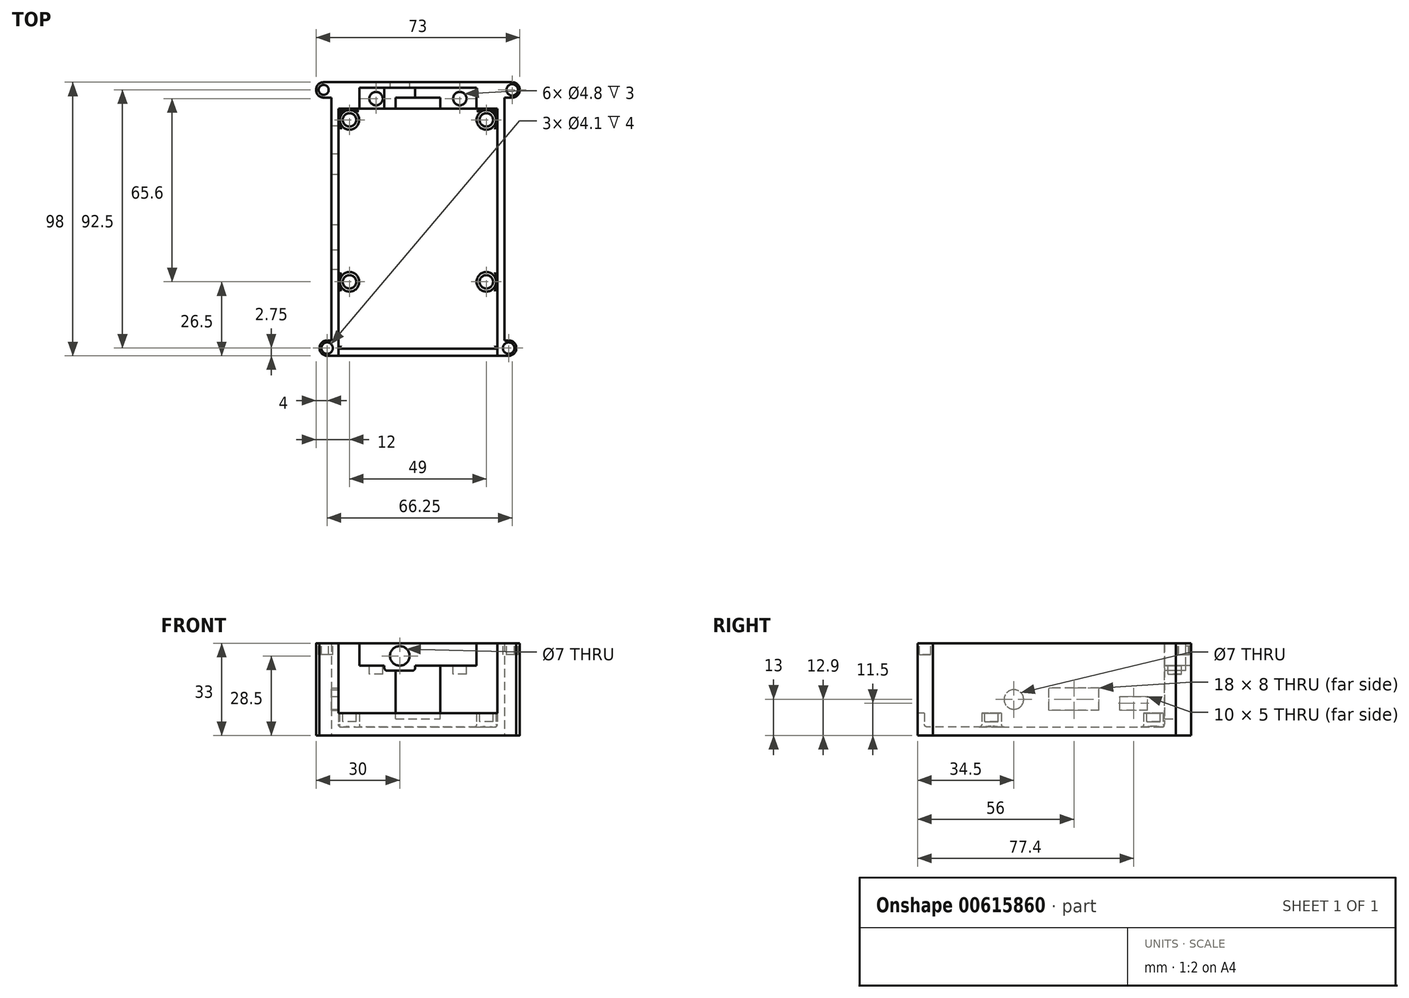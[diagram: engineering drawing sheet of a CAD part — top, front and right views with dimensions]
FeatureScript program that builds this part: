
annotation { "Feature Type Name" : "Feature", "Feature Type Description" : "" }
export const myFeature = defineFeature(function(context is Context, id is Id, definition is map)
    precondition{}
    {
        {
            var Q0;
            Q0=qCreatedBy(makeId("Top.planeOp"),FACE);
            var sketch = newSketch(context, id + "F0", { "sketchPlane" : qUnion([Q0])});
            skLineSegment(sketch, "E0.bottom", {"start": v(25, -42.5) * mm, "end": v(-28, -42.5) * mm, "construction": true});
            skLineSegment(sketch, "E0.top", {"start": v(25, 42.5) * mm, "end": v(-25, 42.5) * mm, "construction": true});
            skLineSegment(sketch, "E0.left", {"start": v(28, -39.5) * mm, "end": v(28, 39.5) * mm, "construction": true});
            skLineSegment(sketch, "E0.right", {"start": v(-28, -42.5) * mm, "end": v(-28, 39.5) * mm, "construction": true});
            skPoint(sketch, "E0.middle", {"position": v(0, 0) * mm});
            skLineSegment(sketch, "E1.0", {"start": v(31, -45.5) * mm, "end": v(-31, -45.5) * mm});
            skLineSegment(sketch, "E1.1", {"start": v(31, -45.5) * mm, "end": v(31, 45.5) * mm});
            skLineSegment(sketch, "E1.2", {"start": v(31, 45.5) * mm, "end": v(-31, 45.5) * mm});
            skLineSegment(sketch, "E1.3", {"start": v(-31, -45.5) * mm, "end": v(-31, 45.5) * mm});
            skPoint(sketch, "E2.visualSharp", {"position": v(28, -42.5) * mm});
            skArc(sketch, "E2.filletArc", {"start": v(25, -42.5) * mm, "mid": v(27.12, -41.62) * mm, "end": v(28, -39.5) * mm, "construction": true});
            skPoint(sketch, "E3.visualSharp", {"position": v(-28, -42.5) * mm});
            skPoint(sketch, "E4.visualSharp", {"position": v(-28, 42.5) * mm});
            skArc(sketch, "E4.filletArc", {"start": v(-25, 42.5) * mm, "mid": v(-27.12, 41.62) * mm, "end": v(-28, 39.5) * mm, "construction": true});
            skPoint(sketch, "E5.visualSharp", {"position": v(28, 42.5) * mm});
            skArc(sketch, "E5.filletArc", {"start": v(28, 39.5) * mm, "mid": v(27.12, 41.62) * mm, "end": v(25, 42.5) * mm, "construction": true});
            skSolve(sketch);
        }
        {
            var Q0;
            Q0 = qSketchRegion(id + "F0", true);
            extrude(context, id + "F1", {"entities" : qUnion([Q0]), "depth" : 3 * mm, "offsetDistance" : 25 * mm});
        }
        {
            var Q0;
            Q0=makeQuery(id+"F1.opExtrude","CAP_FACE",FACE,{"disambiguationData":[OSD([sQuery(id+"F0.wireOp",EDGE,"E1.0"),sQuery(id+"F0.wireOp",EDGE,"E1.1"),sQuery(id+"F0.wireOp",EDGE,"E1.2"),sQuery(id+"F0.wireOp",EDGE,"E1.3")])],"isStart":false});
            var sketch = newSketch(context, id + "F2", { "sketchPlane" : qUnion([Q0])});
            skLineSegment(sketch, "E6.0", {"start": v(-28.5, 43) * mm, "end": v(-28.5, -43) * mm});
            skLineSegment(sketch, "E6.1", {"start": v(28.5, 43) * mm, "end": v(-28.5, 43) * mm});
            skLineSegment(sketch, "E6.2", {"start": v(28.5, -43) * mm, "end": v(28.5, 43) * mm});
            skLineSegment(sketch, "E6.3", {"start": v(-28.5, -43) * mm, "end": v(28.5, -43) * mm});
            skLineSegment(sketch, "E7.bottom", {"start": v(-31, 45.5) * mm, "end": v(31, 45.5) * mm});
            skLineSegment(sketch, "E7.top", {"start": v(-31, -45.5) * mm, "end": v(31, -45.5) * mm});
            skLineSegment(sketch, "E7.left", {"start": v(-31, 45.5) * mm, "end": v(-31, -45.5) * mm});
            skLineSegment(sketch, "E7.right", {"start": v(31, 45.5) * mm, "end": v(31, -45.5) * mm});
            skSolve(sketch);
        }
        {
            var Q0;
            Q0 = qSketchRegion(id + "F2", true);
            extrude(context, id + "F3", {"entities" : qUnion([Q0]), "operationType" : NewBodyOperationType.ADD, "depth" : 30 * mm, "offsetDistance" : 25 * mm});
        }
        {
            var Q0;
            Q0=makeQuery(id+"F1.opExtrude","CAP_FACE",FACE,{"disambiguationData":[OSD([sQuery(id+"F0.wireOp",EDGE,"E1.0"),sQuery(id+"F0.wireOp",EDGE,"E1.1"),sQuery(id+"F0.wireOp",EDGE,"E1.2"),sQuery(id+"F0.wireOp",EDGE,"E1.3")])],"isStart":false});
            var sketch = newSketch(context, id + "F4", { "sketchPlane" : qUnion([Q0])});
            skCircle(sketch, "E8", {"center": v(-24.5, 39) * mm, "radius": 3.5 * mm});
            skCircle(sketch, "E9", {"center": v(24.5, 39) * mm, "radius": 3.5 * mm});
            skCircle(sketch, "E10", {"center": v(-24.5, -19) * mm, "radius": 3.5 * mm});
            skCircle(sketch, "E11", {"center": v(24.5, -19) * mm, "radius": 3.5 * mm});
            skSolve(sketch);
        }
        {
            var Q0;
            Q0 = qSketchRegion(id + "F4", true);
            extrude(context, id + "F5", {"entities" : qUnion([Q0]), "operationType" : NewBodyOperationType.ADD, "depth" : 5 * mm, "offsetDistance" : 25 * mm});
        }
        {
            var Q0;
            Q0=makeQuery(id+"F5.opExtrude","CAP_FACE",FACE,{"disambiguationData":[OSD([sQuery(id+"F4.wireOp",EDGE,"E9")])],"isStart":false});
            var sketch = newSketch(context, id + "F6", { "sketchPlane" : qUnion([Q0])});
            skCircle(sketch, "E12", {"center": v(-24.5, 39) * mm, "radius": 2.4 * mm});
            skCircle(sketch, "E13", {"center": v(24.5, 39) * mm, "radius": 2.4 * mm});
            skCircle(sketch, "E14", {"center": v(-24.5, -19) * mm, "radius": 2.4 * mm});
            skCircle(sketch, "E15", {"center": v(24.5, -19) * mm, "radius": 2.4 * mm});
            skSolve(sketch);
        }
        {
            var Q0;
            Q0 = qSketchRegion(id + "F6", true);
            extrude(context, id + "F7", {"entities" : qUnion([Q0]), "operationType" : NewBodyOperationType.REMOVE, "oppositeDirection" : true, "depth" : 3 * mm, "offsetDistance" : 25 * mm});
        }
        {
            var Q0;
            Q0=makeQuery(id+"F3.boolean.opBoolean","MERGE",FACE,{"derivedFrom":[makeQuery(id+"F1.opExtrude","SWEPT_FACE",FACE,{"disambiguationData":[OSD([sQuery(id+"F0.wireOp",EDGE,"E1.0")])]}),makeQuery(id+"F3.opExtrude","SWEPT_FACE",FACE,{"disambiguationData":[OSD([sQuery(id+"F2.wireOp",EDGE,"E7.top")])]})]});
            var sketch = newSketch(context, id + "F8", { "sketchPlane" : qUnion([Q0])});
            skLineSegment(sketch, "E16", {"start": v(-28.5, 8) * mm, "end": v(28.5, 8) * mm});
            skLineSegment(sketch, "E17", {"start": v(28.5, 8) * mm, "end": v(28.5, 33) * mm});
            skLineSegment(sketch, "E18", {"start": v(-28.5, 8) * mm, "end": v(-28.5, 33) * mm});
            skLineSegment(sketch, "E19", {"start": v(28.5, 33) * mm, "end": v(-28.5, 33) * mm});
            skSolve(sketch);
        }
        {
            var Q0;
            Q0 = qSketchRegion(id + "F8", true);
            var Q1;
            Q1=makeQuery(id+"F3.opExtrude","SWEPT_FACE",FACE,{"disambiguationData":[OSD([sQuery(id+"F2.wireOp",EDGE,"E6.3")])]});
            extrude(context, id + "F9", {"entities" : qUnion([Q0]), "operationType" : NewBodyOperationType.REMOVE, "endBound" : BoundingType.UP_TO_SURFACE, "oppositeDirection" : true, "depth" : 25 * mm, "endBoundEntityFace" : qUnion([Q1]), "offsetDistance" : 25 * mm});
        }
        {
            var Q0;
            Q0=makeQuery(id+"F3.opExtrude","SWEPT_FACE",FACE,{"disambiguationData":[OSD([sQuery(id+"F2.wireOp",EDGE,"E6.0")])]});
            var sketch = newSketch(context, id + "F10", { "sketchPlane" : qUnion([Q0])});
            skLineSegment(sketch, "E20.bottom", {"start": v(36.9, 9) * mm, "end": v(26.9, 9) * mm});
            skLineSegment(sketch, "E20.left", {"start": v(36.9, 9) * mm, "end": v(36.9, 14) * mm});
            skLineSegment(sketch, "E20.right", {"start": v(26.9, 9) * mm, "end": v(26.9, 14) * mm});
            skLineSegment(sketch, "E21", {"start": v(42.5, 25.13) * mm, "end": v(42.5, 0) * mm, "construction": true});
            skLineSegment(sketch, "E22.bottom", {"start": v(19.5, 9) * mm, "end": v(1.5, 9) * mm});
            skLineSegment(sketch, "E22.top", {"start": v(19.5, 17) * mm, "end": v(1.5, 17) * mm});
            skLineSegment(sketch, "E22.left", {"start": v(19.5, 9) * mm, "end": v(19.5, 17) * mm});
            skLineSegment(sketch, "E22.right", {"start": v(1.5, 9) * mm, "end": v(1.5, 17) * mm});
            skLineSegment(sketch, "E23", {"start": v(26.9, 14) * mm, "end": v(31.9, 14) * mm});
            skLineSegment(sketch, "E24", {"start": v(31.9, 14) * mm, "end": v(36.9, 14) * mm});
            skLineSegment(sketch, "E25", {"start": v(10.5, 17) * mm, "end": v(10.5, 23.95) * mm, "construction": true});
            skPoint(sketch, "E25.endSnap0", {"position": v(10.5, 17) * mm});
            skLineSegment(sketch, "E26", {"start": v(26.9, 9) * mm, "end": v(19.5, 9) * mm, "construction": true});
            skCircle(sketch, "E27", {"center": v(-11, 12.9) * mm, "radius": 3.5 * mm});
            skSolve(sketch);
        }
        {
            var Q0;
            Q0 = qSketchRegion(id + "F10", true);
            var Q1;
            Q1=makeQuery(id+"F3.boolean.opBoolean","MERGE",FACE,{"derivedFrom":[makeQuery(id+"F1.opExtrude","SWEPT_FACE",FACE,{"disambiguationData":[OSD([sQuery(id+"F0.wireOp",EDGE,"E1.3")])]}),makeQuery(id+"F3.opExtrude","SWEPT_FACE",FACE,{"disambiguationData":[OSD([sQuery(id+"F2.wireOp",EDGE,"E7.left")])]})]});
            extrude(context, id + "F11", {"entities" : qUnion([Q0]), "operationType" : NewBodyOperationType.REMOVE, "endBound" : BoundingType.UP_TO_SURFACE, "oppositeDirection" : true, "depth" : 25 * mm, "endBoundEntityFace" : qUnion([Q1]), "offsetDistance" : 25 * mm});
        }
        {
            var Q0;
            Q0=makeQuery(id+"F3.boolean.opBoolean","MERGE",FACE,{"derivedFrom":[makeQuery(id+"F1.opExtrude","SWEPT_FACE",FACE,{"disambiguationData":[OSD([sQuery(id+"F0.wireOp",EDGE,"E1.2")])]}),makeQuery(id+"F3.opExtrude","SWEPT_FACE",FACE,{"disambiguationData":[OSD([sQuery(id+"F2.wireOp",EDGE,"E7.bottom")])]})]});
            extrude(context, id + "F12", {"entities" : qUnion([Q0]), "operationType" : NewBodyOperationType.ADD, "depth" : 7 * mm, "offsetDistance" : 25 * mm});
        }
        {
            var Q0;
            {var subQ0=sQuery(id+"F2.wireOp",EDGE,"E7.bottom");Q0=makeQuery(id+"F12.boolean.opBoolean","MERGE",FACE,{"derivedFrom":[makeQuery(id+"F3.opExtrude","CAP_FACE",FACE,{"disambiguationData":[OSD([sQuery(id+"F2.wireOp",EDGE,"E6.0"),sQuery(id+"F2.wireOp",EDGE,"E6.1"),sQuery(id+"F2.wireOp",EDGE,"E6.2"),sQuery(id+"F2.wireOp",EDGE,"E6.3"),subQ0,sQuery(id+"F2.wireOp",EDGE,"E7.top"),sQuery(id+"F2.wireOp",EDGE,"E7.left"),sQuery(id+"F2.wireOp",EDGE,"E7.right")])],"isStart":false}),makeQuery(id+"F12.opExtrude","SWEPT_FACE",FACE,{"disambiguationData":[OSD([subQ0])]})]});}
            var sketch = newSketch(context, id + "F13", { "sketchPlane" : qUnion([Q0])});
            skLineSegment(sketch, "E28", {"start": v(-21, 43) * mm, "end": v(-21, 50.5) * mm});
            skLineSegment(sketch, "E29", {"start": v(-21, 50.5) * mm, "end": v(21, 50.5) * mm});
            skLineSegment(sketch, "E30", {"start": v(21, 50.5) * mm, "end": v(21, 43) * mm});
            skLineSegment(sketch, "E31", {"start": v(-21, 43) * mm, "end": v(21, 43) * mm});
            skSolve(sketch);
        }
        {
            var Q0;
            Q0 = qSketchRegion(id + "F13", true);
            extrude(context, id + "F14", {"entities" : qUnion([Q0]), "operationType" : NewBodyOperationType.REMOVE, "oppositeDirection" : true, "depth" : 8 * mm, "offsetDistance" : 25 * mm});
        }
        {
            var Q0;
            Q0=makeQuery(id+"F14.boolean.opBoolean","COPY",FACE,{"derivedFrom":makeQuery(id+"F14.opExtrude","CAP_FACE",FACE,{"disambiguationData":[OSD([sQuery(id+"F13.wireOp",EDGE,"E28"),sQuery(id+"F13.wireOp",EDGE,"E29"),sQuery(id+"F13.wireOp",EDGE,"E30"),sQuery(id+"F13.wireOp",EDGE,"Brvc21Z0-0QBP-XG2K-26vJ-c9HecIgVGcnL")])],"isStart":false})});
            var sketch = newSketch(context, id + "F15", { "sketchPlane" : qUnion([Q0])});
            skCircle(sketch, "E32", {"center": v(-15, 46.6) * mm, "radius": 2.4 * mm});
            skCircle(sketch, "E33", {"center": v(15, 46.6) * mm, "radius": 2.4 * mm});
            skLineSegment(sketch, "E34", {"start": v(15, 46.6) * mm, "end": v(-15, 46.6) * mm, "construction": true});
            skSolve(sketch);
        }
        {
            var Q0;
            Q0 = qSketchRegion(id + "F15", true);
            extrude(context, id + "F16", {"entities" : qUnion([Q0]), "operationType" : NewBodyOperationType.REMOVE, "oppositeDirection" : true, "depth" : 3 * mm, "offsetDistance" : 25 * mm});
        }
        {
            var Q0;
            Q0=makeQuery(id+"F14.boolean.opBoolean","COPY",FACE,{"derivedFrom":makeQuery(id+"F14.opExtrude","CAP_FACE",FACE,{"disambiguationData":[OSD([sQuery(id+"F13.wireOp",EDGE,"E28"),sQuery(id+"F13.wireOp",EDGE,"E29"),sQuery(id+"F13.wireOp",EDGE,"E30"),sQuery(id+"F13.wireOp",EDGE,"E31")])],"isStart":false})});
            var sketch = newSketch(context, id + "F17", { "sketchPlane" : qUnion([Q0])});
            skLineSegment(sketch, "E35.bottom", {"start": v(-12, 50.5) * mm, "end": v(-1, 50.5) * mm});
            skLineSegment(sketch, "E35.top", {"start": v(-12, 43) * mm, "end": v(-1, 43) * mm});
            skLineSegment(sketch, "E35.left", {"start": v(-12, 50.5) * mm, "end": v(-12, 43) * mm});
            skLineSegment(sketch, "E35.right", {"start": v(-1, 50.5) * mm, "end": v(-1, 43) * mm});
            skSolve(sketch);
        }
        {
            var Q0;
            Q0 = qSketchRegion(id + "F17", true);
            extrude(context, id + "F18", {"entities" : qUnion([Q0]), "operationType" : NewBodyOperationType.REMOVE, "oppositeDirection" : true, "depth" : 1.8 * mm, "offsetDistance" : 25 * mm});
        }
        {
            var Q0;
            Q0=makeQuery(id+"F18.boolean.opBoolean","COPY",EDGE,{"derivedFrom":makeQuery(id+"F18.opExtrude","CAP_EDGE",EDGE,{"disambiguationData":[OSD([sQuery(id+"F17.wireOp",EDGE,"E35.left")])],"isStart":false})});
            var Q1;
            Q1=makeQuery(id+"F18.boolean.opBoolean","COPY",EDGE,{"derivedFrom":makeQuery(id+"F18.opExtrude","CAP_EDGE",EDGE,{"disambiguationData":[OSD([sQuery(id+"F17.wireOp",EDGE,"E35.right")])],"isStart":false})});
            fillet(context, id + "F19", {"entities" : qUnion([Q0, Q1]), "radius" : 1 * mm, "tangentPropagation" : true, "allowEdgeOverflow" : false});
        }
        {
            var Q0;
            Q0=makeQuery(id+"F18.boolean.opBoolean","MERGE",FACE,{"derivedFrom":[makeQuery(id+"F14.boolean.opBoolean","COPY",FACE,{"derivedFrom":makeQuery(id+"F14.opExtrude","SWEPT_FACE",FACE,{"disambiguationData":[OSD([sQuery(id+"F13.wireOp",EDGE,"E29")])]})}),makeQuery(id+"F18.opExtrude","SWEPT_FACE",FACE,{"disambiguationData":[OSD([sQuery(id+"F17.wireOp",EDGE,"E35.bottom")])]})]});
            var sketch = newSketch(context, id + "F20", { "sketchPlane" : qUnion([Q0])});
            skCircle(sketch, "E36", {"center": v(-6.5, 28.5) * mm, "radius": 3.5 * mm});
            skLineSegment(sketch, "E37", {"start": v(-12, 25) * mm, "end": v(-1, 25) * mm, "construction": true});
            skLineSegment(sketch, "E38", {"start": v(-6.5, 23.2) * mm, "end": v(-6.5, 28.5) * mm, "construction": true});
            skSolve(sketch);
        }
        {
            var Q0;
            Q0 = qSketchRegion(id + "F20", true);
            var Q1;
            Q1=makeQuery(id+"F12.opExtrude","CAP_FACE",FACE,{"disambiguationData":[OSD([sQuery(id+"F0.wireOp",EDGE,"E1.2"),sQuery(id+"F2.wireOp",EDGE,"E7.bottom")])],"isStart":false});
            extrude(context, id + "F21", {"entities" : qUnion([Q0]), "operationType" : NewBodyOperationType.REMOVE, "endBound" : BoundingType.UP_TO_SURFACE, "oppositeDirection" : true, "depth" : 25 * mm, "endBoundEntityFace" : qUnion([Q1]), "offsetDistance" : 25 * mm});
        }
        {
            var Q0;
            Q0=makeQuery(id+"F5.opExtrude","CAP_EDGE",EDGE,{"disambiguationData":[OSD([sQuery(id+"F4.wireOp",EDGE,"E9")])],"isStart":true});
            var Q1;
            Q1=makeQuery(id+"F3.opExtrude","CAP_EDGE",EDGE,{"disambiguationData":[OSD([sQuery(id+"F2.wireOp",EDGE,"E6.1")])],"isStart":true});
            var Q2;
            Q2=makeQuery(id+"F5.opExtrude","CAP_EDGE",EDGE,{"disambiguationData":[OSD([sQuery(id+"F4.wireOp",EDGE,"E8")])],"isStart":true});
            var Q3;
            Q3=makeQuery(id+"F5.opExtrude","CAP_EDGE",EDGE,{"disambiguationData":[OSD([sQuery(id+"F4.wireOp",EDGE,"E10")])],"isStart":true});
            var Q4;
            Q4=makeQuery(id+"F5.opExtrude","CAP_EDGE",EDGE,{"disambiguationData":[OSD([sQuery(id+"F4.wireOp",EDGE,"E11")])],"isStart":true});
            var Q5;
            Q5=makeQuery(id+"F1.opExtrude","CAP_FACE",FACE,{"disambiguationData":[OSD([sQuery(id+"F0.wireOp",EDGE,"E1.0"),sQuery(id+"F0.wireOp",EDGE,"E1.1"),sQuery(id+"F0.wireOp",EDGE,"E1.2"),sQuery(id+"F0.wireOp",EDGE,"E1.3")])],"isStart":false});
            fillet(context, id + "F22", {"entities" : qUnion([Q0, Q1, Q2, Q3, Q4, Q5]), "radius" : 1 * mm, "tangentPropagation" : true, "allowEdgeOverflow" : false});
        }
        {
            var Q0;
            Q0=makeQuery(id+"F0.imprint","IMPRINT",FACE,{"disambiguationData":[TD([[makeQuery(id+"F0.imprint","IMPRINT",EDGE,{"derivedFrom":sQuery(id+"F0.wireOp",EDGE,"E1.0")}),-1.0]])]});
            var sketch = newSketch(context, id + "F23", { "sketchPlane" : qUnion([Q0])});
            skCircle(sketch, "E39", {"center": v(32.5, -42.75) * mm, "radius": 1.5 * mm, "construction": true});
            skArc(sketch, "E40", {"start": v(32.5, -45.5) * mm, "mid": v(35.25, -42.75) * mm, "end": v(32.5, -40) * mm});
            skLineSegment(sketch, "E41", {"start": v(31, -45.5) * mm, "end": v(32.5, -45.5) * mm});
            skLineSegment(sketch, "E42", {"start": v(31, -40) * mm, "end": v(32.5, -40) * mm});
            skLineSegment(sketch, "E43", {"start": v(31, -40) * mm, "end": v(31, -45.5) * mm});
            skCircle(sketch, "E44", {"center": v(-32.5, -42.75) * mm, "radius": 1.5 * mm, "construction": true});
            skArc(sketch, "E45", {"start": v(-32.5, -40) * mm, "mid": v(-35.25, -42.75) * mm, "end": v(-32.5, -45.5) * mm});
            skLineSegment(sketch, "E46", {"start": v(-31, -45.5) * mm, "end": v(-32.5, -45.5) * mm});
            skLineSegment(sketch, "E47", {"start": v(-31, -40) * mm, "end": v(-32.5, -40) * mm});
            skLineSegment(sketch, "E48", {"start": v(-31, -40) * mm, "end": v(-31, -45.5) * mm});
            skCircle(sketch, "E49", {"center": v(-33.75, 49.75) * mm, "radius": 1.5 * mm, "construction": true});
            skArc(sketch, "E50", {"start": v(-33.75, 52.5) * mm, "mid": v(-36.5, 49.75) * mm, "end": v(-33.75, 47) * mm});
            skLineSegment(sketch, "E51", {"start": v(-31, 52.5) * mm, "end": v(-33.75, 52.5) * mm});
            skLineSegment(sketch, "E52", {"start": v(-31, 47) * mm, "end": v(-33.75, 47) * mm});
            skArc(sketch, "E53", {"start": v(33.75, 47) * mm, "mid": v(36.5, 49.75) * mm, "end": v(33.75, 52.5) * mm});
            skLineSegment(sketch, "E54", {"start": v(31, 52.5) * mm, "end": v(33.75, 52.5) * mm});
            skLineSegment(sketch, "E55", {"start": v(31, 47) * mm, "end": v(33.75, 47) * mm});
            skCircle(sketch, "E56", {"center": v(33.75, 49.75) * mm, "radius": 1.5 * mm, "construction": true});
            skLineSegment(sketch, "E57", {"start": v(31, 47) * mm, "end": v(31, 52.5) * mm});
            skLineSegment(sketch, "E58", {"start": v(-31, 47) * mm, "end": v(-31, 52.5) * mm});
            skSolve(sketch);
        }
        {
            var Q0;
            Q0 = qSketchRegion(id + "F23", true);
            var Q1;
            {var subQ0=sQuery(id+"F2.wireOp",EDGE,"E7.bottom");Q1=makeQuery(id+"F12.boolean.opBoolean","MERGE",FACE,{"derivedFrom":[makeQuery(id+"F3.opExtrude","CAP_FACE",FACE,{"disambiguationData":[OSD([sQuery(id+"F2.wireOp",EDGE,"E6.0"),sQuery(id+"F2.wireOp",EDGE,"E6.1"),sQuery(id+"F2.wireOp",EDGE,"E6.2"),sQuery(id+"F2.wireOp",EDGE,"E6.3"),subQ0,sQuery(id+"F2.wireOp",EDGE,"E7.top"),sQuery(id+"F2.wireOp",EDGE,"E7.left"),sQuery(id+"F2.wireOp",EDGE,"E7.right")])],"isStart":false}),makeQuery(id+"F12.opExtrude","SWEPT_FACE",FACE,{"disambiguationData":[OSD([subQ0])]})]});}
            extrude(context, id + "F24", {"entities" : qUnion([Q0]), "operationType" : NewBodyOperationType.ADD, "endBound" : BoundingType.UP_TO_SURFACE, "depth" : 25 * mm, "endBoundEntityFace" : qUnion([Q1]), "offsetDistance" : 25 * mm});
        }
        {
            var Q0;
            {var subQ0=sQuery(id+"F2.wireOp",EDGE,"E7.right");var subQ1=sQuery(id+"F2.wireOp",EDGE,"E7.left");var subQ2=sQuery(id+"F2.wireOp",EDGE,"E7.top");var subQ3=sQuery(id+"F2.wireOp",EDGE,"E7.bottom");var subQ4=sQuery(id+"F2.wireOp",EDGE,"E6.3");var subQ5=sQuery(id+"F2.wireOp",EDGE,"E6.2");var subQ6=sQuery(id+"F2.wireOp",EDGE,"E6.1");var subQ7=sQuery(id+"F2.wireOp",EDGE,"E6.0");Q0=makeQuery(id+"F24.boolean.opBoolean","MERGE",FACE,{"derivedFrom":[makeQuery(id+"F12.boolean.opBoolean","MERGE",FACE,{"derivedFrom":[makeQuery(id+"F3.opExtrude","CAP_FACE",FACE,{"disambiguationData":[OSD([subQ7,subQ6,subQ5,subQ4,subQ3,subQ2,subQ1,subQ0])],"isStart":false}),makeQuery(id+"F12.opExtrude","SWEPT_FACE",FACE,{"disambiguationData":[OSD([subQ3])]})]}),makeQuery(id+"F24.opExtrude","CAP_FACE",FACE,{"disambiguationData":[OSD([subQ7,subQ6,subQ5,subQ4,subQ3,subQ2,subQ1,subQ0]),OD(0.0)],"isStart":false}),makeQuery(id+"F24.opExtrude","CAP_FACE",FACE,{"disambiguationData":[OSD([subQ7,subQ6,subQ5,subQ4,subQ3,subQ2,subQ1,subQ0]),OD(1.0)],"isStart":false})]});}
            var sketch = newSketch(context, id + "F25", { "sketchPlane" : qUnion([Q0])});
            skCircle(sketch, "E59", {"center": v(-32.5, -42.75) * mm, "radius": 2.05 * mm});
            skCircle(sketch, "E60", {"center": v(32.5, -42.75) * mm, "radius": 2.05 * mm});
            skCircle(sketch, "E61", {"center": v(-33.75, 49.75) * mm, "radius": 1.8 * mm});
            skCircle(sketch, "E62", {"center": v(33.75, 49.75) * mm, "radius": 2.05 * mm});
            skSolve(sketch);
        }
        {
            var Q0;
            Q0 = qSketchRegion(id + "F25", true);
            extrude(context, id + "F26", {"entities" : qUnion([Q0]), "operationType" : NewBodyOperationType.REMOVE, "oppositeDirection" : true, "depth" : 4 * mm, "offsetDistance" : 25 * mm});
        }
        {
            var Q0;
            {var subQ0=sQuery(id+"F13.wireOp",EDGE,"E30");var subQ1=sQuery(id+"F13.wireOp",EDGE,"E29");Q0=makeQuery(id+"F18.boolean.opBoolean","SPLIT",FACE,{"disambiguationData":[TD([makeQuery(id+"F14.boolean.opBoolean","COPY",FACE,{"derivedFrom":makeQuery(id+"F14.opExtrude","SWEPT_FACE",FACE,{"disambiguationData":[OSD([subQ0])]})})])],"derivedFrom":makeQuery(id+"F14.boolean.opBoolean","COPY",FACE,{"derivedFrom":makeQuery(id+"F14.opExtrude","CAP_FACE",FACE,{"disambiguationData":[OSD([sQuery(id+"F13.wireOp",EDGE,"E28"),subQ1,subQ0,sQuery(id+"F13.wireOp",EDGE,"E31")])],"isStart":false})})});}
            var sketch = newSketch(context, id + "F27", { "sketchPlane" : qUnion([Q0])});
            skLineSegment(sketch, "E63.bottom", {"start": v(8, 43) * mm, "end": v(-8, 43) * mm});
            skLineSegment(sketch, "E64", {"start": v(8, 43) * mm, "end": v(8, 47) * mm});
            skLineSegment(sketch, "E65", {"start": v(-21, 50.5) * mm, "end": v(21, 50.5) * mm, "construction": true});
            skLineSegment(sketch, "E66", {"start": v(0, 50.5) * mm, "end": v(0, 47) * mm, "construction": true});
            skLineSegment(sketch, "E67", {"start": v(0, 47) * mm, "end": v(8, 47) * mm});
            skLineSegment(sketch, "E68", {"start": v(0, 47) * mm, "end": v(-8, 47) * mm});
            skLineSegment(sketch, "E69", {"start": v(-8, 47) * mm, "end": v(-8, 43) * mm});
            skSolve(sketch);
        }
        {
            var Q0;
            Q0 = qSketchRegion(id + "F27", true);
            var Q1;
            Q1=makeQuery(id+"F5.opExtrude","CAP_FACE",FACE,{"disambiguationData":[OSD([sQuery(id+"F4.wireOp",EDGE,"E8")])],"isStart":false});
            extrude(context, id + "F28", {"entities" : qUnion([Q0]), "operationType" : NewBodyOperationType.REMOVE, "endBound" : BoundingType.UP_TO_SURFACE, "oppositeDirection" : true, "depth" : 16.2 * mm, "endBoundEntityFace" : qUnion([Q1]), "hasOffset" : true, "offsetDistance" : 2 * mm, "offsetOppositeDirection" : true});
        }
    });
